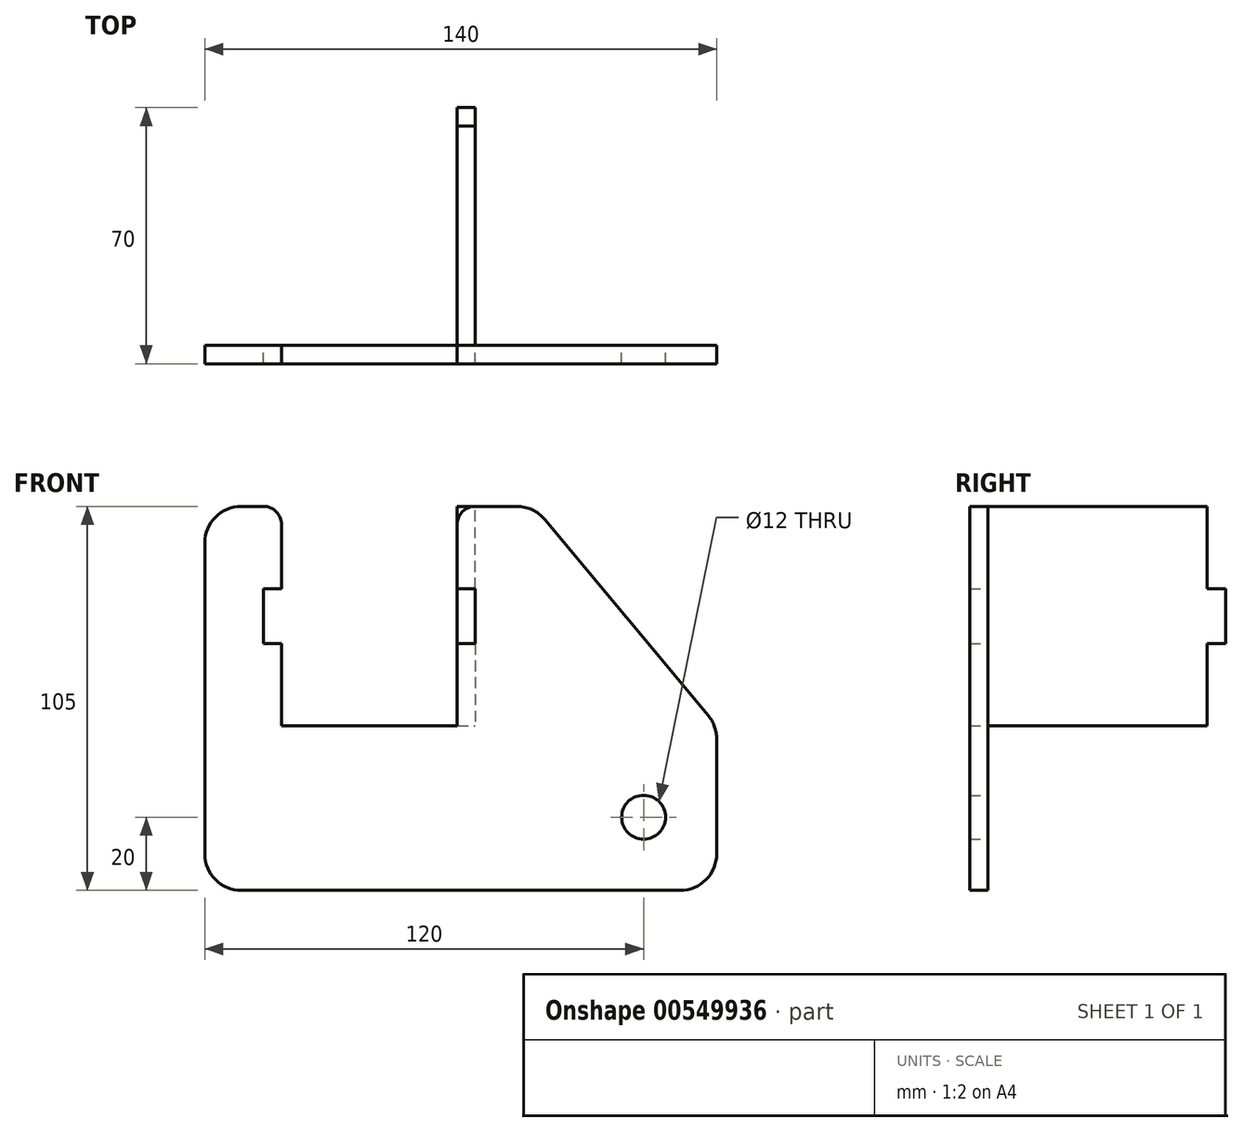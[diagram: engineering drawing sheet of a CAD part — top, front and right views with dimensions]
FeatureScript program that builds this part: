
annotation { "Feature Type Name" : "Feature", "Feature Type Description" : "" }
export const myFeature = defineFeature(function(context is Context, id is Id, definition is map)
    precondition{}
    {
        {
            var Q0;
            Q0=qCreatedBy(makeId("Front.planeOp"),FACE);
            var sketch = newSketch(context, id + "F0", { "sketchPlane" : qUnion([Q0])});
            skLineSegment(sketch, "E0", {"start": v(10, 0) * mm, "end": v(130, 0) * mm});
            skLineSegment(sketch, "E1", {"start": v(0, 10) * mm, "end": v(0, 95) * mm});
            skLineSegment(sketch, "E2", {"start": v(10, 105) * mm, "end": v(16, 105) * mm});
            skLineSegment(sketch, "E3", {"start": v(93, 101.4) * mm, "end": v(137.68, 47.78) * mm});
            skLineSegment(sketch, "E4", {"start": v(140, 41.38) * mm, "end": v(140, 10) * mm});
            skPoint(sketch, "E5", {"position": v(21, 45) * mm});
            skPoint(sketch, "E6", {"position": v(45, 105) * mm});
            skLineSegment(sketch, "E7", {"start": v(21, 45) * mm, "end": v(21, 100) * mm});
            skLineSegment(sketch, "E8", {"start": v(21, 45) * mm, "end": v(69, 45) * mm});
            skLineSegment(sketch, "E9", {"start": v(69, 45) * mm, "end": v(69, 100) * mm});
            skPoint(sketch, "E10", {"position": v(21, 75) * mm});
            skLineSegment(sketch, "E11", {"start": v(21, 75) * mm, "end": v(21, 82.5) * mm});
            skLineSegment(sketch, "E12", {"start": v(21, 82.5) * mm, "end": v(16, 82.5) * mm});
            skLineSegment(sketch, "E13", {"start": v(16, 82.5) * mm, "end": v(16, 67.5) * mm});
            skLineSegment(sketch, "E14", {"start": v(16, 67.5) * mm, "end": v(21, 67.5) * mm});
            skLineSegment(sketch, "E15", {"start": v(45, 105) * mm, "end": v(45, 45) * mm, "construction": true});
            skLineSegment(sketch, "E16.MirrorCS", {"start": v(69, 82.5) * mm, "end": v(74, 82.5) * mm});
            skLineSegment(sketch, "E17.MirrorCS", {"start": v(74, 82.5) * mm, "end": v(74, 67.5) * mm});
            skLineSegment(sketch, "E18.MirrorCS", {"start": v(74, 67.5) * mm, "end": v(69, 67.5) * mm});
            skPoint(sketch, "E19.visualSharp", {"position": v(90, 105) * mm});
            skArc(sketch, "E19.filletArc", {"start": v(93, 101.4) * mm, "mid": v(89.56, 104.06) * mm, "end": v(85.32, 105) * mm});
            skPoint(sketch, "E20.visualSharp", {"position": v(0, 105) * mm});
            skArc(sketch, "E20.filletArc", {"start": v(10, 105) * mm, "mid": v(2.93, 102.07) * mm, "end": v(0, 95) * mm});
            skPoint(sketch, "E21.visualSharp", {"position": v(0, 0) * mm});
            skArc(sketch, "E21.filletArc", {"start": v(0, 10) * mm, "mid": v(2.93, 2.93) * mm, "end": v(10, 0) * mm});
            skPoint(sketch, "E22.visualSharp", {"position": v(140, 0) * mm});
            skArc(sketch, "E22.filletArc", {"start": v(130, 0) * mm, "mid": v(137.07, 2.93) * mm, "end": v(140, 10) * mm});
            skPoint(sketch, "E23.visualSharp", {"position": v(140, 45) * mm});
            skArc(sketch, "E23.filletArc", {"start": v(140, 41.38) * mm, "mid": v(139.4, 44.78) * mm, "end": v(137.68, 47.78) * mm});
            skPoint(sketch, "E24", {"position": v(120, 20) * mm});
            skCircle(sketch, "E25", {"center": v(120, 20) * mm, "radius": 6 * mm});
            skLineSegment(sketch, "E26.trimOffspring", {"start": v(74, 105) * mm, "end": v(85.32, 105) * mm});
            skPoint(sketch, "E27.visualSharp", {"position": v(21, 105) * mm});
            skArc(sketch, "E27.filletArc", {"start": v(21, 100) * mm, "mid": v(19.54, 103.54) * mm, "end": v(16, 105) * mm});
            skPoint(sketch, "E28.visualSharp", {"position": v(69, 105) * mm});
            skArc(sketch, "E28.filletArc", {"start": v(74, 105) * mm, "mid": v(70.46, 103.54) * mm, "end": v(69, 100) * mm});
            skSolve(sketch);
        }
        {
            var Q0;
            Q0=makeQuery(id+"F0.imprint","IMPRINT",FACE,{"disambiguationData":[TD([[makeQuery(id+"F0.imprint","IMPRINT",EDGE,{"derivedFrom":sQuery(id+"F0.wireOp",EDGE,"E0")}),1.0]])]});
            extrude(context, id + "F1", {"entities" : qUnion([Q0]), "depth" : 5 * mm});
        }
        {
            var Q0;
            Q0=makeQuery(id+"F1.opExtrude","SWEPT_FACE",FACE,{"disambiguationData":[OSD([sQuery(id+"F0.wireOp",EDGE,"E17.MirrorCS")])]});
            var sketch = newSketch(context, id + "F2", { "sketchPlane" : qUnion([Q0])});
            skLineSegment(sketch, "E29.0", {"start": v(5, 82.5) * mm, "end": v(5, 67.5) * mm});
            skLineSegment(sketch, "E30.0.1", {"start": v(0, 82.5) * mm, "end": v(5, 82.5) * mm});
            skLineSegment(sketch, "E30.0.3", {"start": v(5, 82.5) * mm, "end": v(0, 82.5) * mm});
            skLineSegment(sketch, "E31.0", {"start": v(5, 67.5) * mm, "end": v(0, 67.5) * mm});
            skLineSegment(sketch, "E32", {"start": v(0, 82.5) * mm, "end": v(0, 105) * mm});
            skLineSegment(sketch, "E33", {"start": v(0, 105) * mm, "end": v(-60, 105) * mm});
            skLineSegment(sketch, "E34", {"start": v(-60, 105) * mm, "end": v(-60, 45) * mm});
            skLineSegment(sketch, "E35", {"start": v(-60, 45) * mm, "end": v(0, 45) * mm});
            skLineSegment(sketch, "E36", {"start": v(0, 45) * mm, "end": v(0, 67.5) * mm});
            skLineSegment(sketch, "E37", {"start": v(-30, 105) * mm, "end": v(-30, 45) * mm, "construction": true});
            skLineSegment(sketch, "E38.MirrorCS", {"start": v(-65, 82.5) * mm, "end": v(-65, 67.5) * mm});
            skLineSegment(sketch, "E39.MirrorCS", {"start": v(-65, 67.5) * mm, "end": v(-60, 67.5) * mm});
            skLineSegment(sketch, "E40.MirrorCS", {"start": v(-65, 82.5) * mm, "end": v(-60, 82.5) * mm});
            skSolve(sketch);
        }
        {
            var Q0;
            Q0=qSketchRegion(id+"F2",true);
            extrude(context, id + "F3", {"entities" : qUnion([Q0]), "depth" : 5 * mm});
        }
    });
